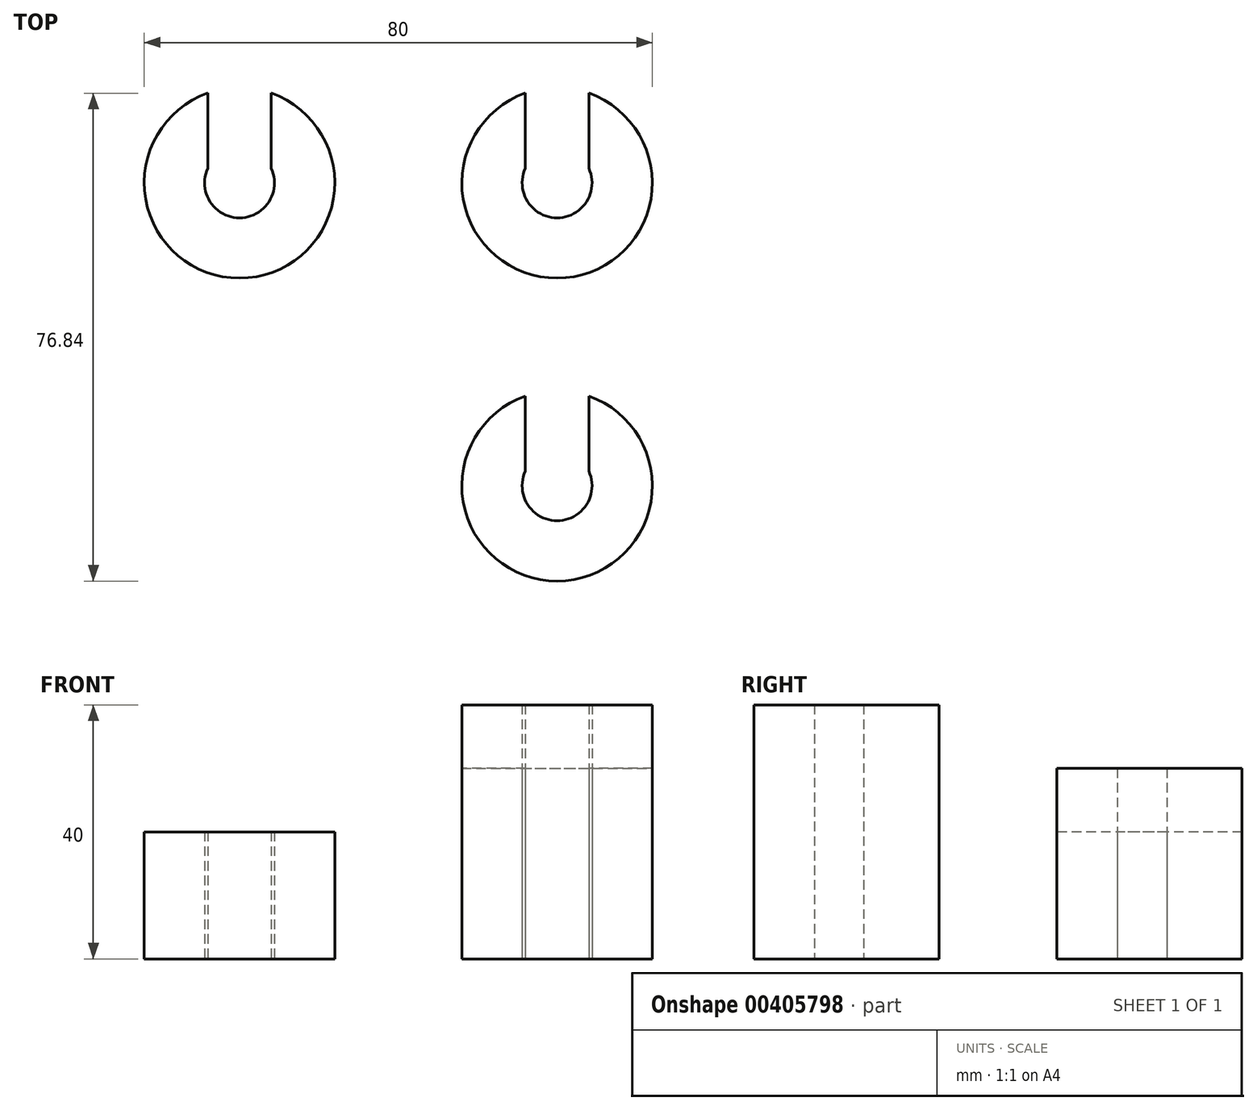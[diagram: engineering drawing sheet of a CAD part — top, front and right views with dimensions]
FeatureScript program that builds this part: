
annotation { "Feature Type Name" : "Feature", "Feature Type Description" : "" }
export const myFeature = defineFeature(function(context is Context, id is Id, definition is map)
    precondition{}
    {
        {
            var Q0;
            Q0=qCreatedBy(makeId("Top.planeOp"),FACE);
            var sketch = newSketch(context, id + "F0", { "sketchPlane" : qUnion([Q0])});
            skCircle(sketch, "E0", {"center": v(0, 0) * mm, "radius": 15 * mm});
            skCircle(sketch, "E1", {"center": v(0, 0) * mm, "radius": 5.5 * mm});
            skLineSegment(sketch, "E2", {"start": v(0, 0) * mm, "end": v(0, 15) * mm, "construction": true});
            skLineSegment(sketch, "E3", {"start": v(5, 15) * mm, "end": v(5, 2.3) * mm});
            skLineSegment(sketch, "E4", {"start": v(-5, 15) * mm, "end": v(-5, 2.3) * mm});
            skLineSegment(sketch, "E5", {"start": v(-5, 15) * mm, "end": v(5, 15) * mm});
            skSolve(sketch);
        }
        {
            var Q0;
            {var subQ0=sQuery(id+"F0.wireOp",EDGE,"E3");var subQ1=sQuery(id+"F0.wireOp",EDGE,"E0");var subQ2=makeQuery(id+"F0.imprint","INTERSECT",VERTEX,{"derivedFrom":[subQ1,subQ0]});Q0=makeQuery(id+"F0.imprint","IMPRINT",FACE,{"disambiguationData":[TD([[makeQuery(id+"F0.imprint","IMPRINT",EDGE,{"disambiguationData":[TD([[subQ2,1.0]])],"derivedFrom":subQ1}),1.0]])]});}
            extrude(context, id + "F1", {"entities" : qUnion([Q0]), "depth" : 20 * mm});
        }
        {
            var Q0;
            Q0=makeQuery(id+"F1.opExtrude","SWEPT_BODY",BODY,{"disambiguationData":[OSD([sQuery(id+"F0.wireOp",EDGE,"E0"),sQuery(id+"F0.wireOp",EDGE,"E1"),sQuery(id+"F0.wireOp",EDGE,"E3"),sQuery(id+"F0.wireOp",EDGE,"E4")])]});
            transform(context, id + "F2", {"entities" : qUnion([Q0]), "transformType" : TransformType.TRANSLATION_3D, "dx" : 50 * mm, "dy" : 0 * mm, "dz" : 0 * mm, "makeCopy" : true});
        }
        {
            var Q0;
            Q0=makeQuery(id+"F2.opPattern","COPY",FACE,{"derivedFrom":makeQuery(id+"F1.opExtrude","CAP_FACE",FACE,{"disambiguationData":[OSD([sQuery(id+"F0.wireOp",EDGE,"E0"),sQuery(id+"F0.wireOp",EDGE,"E1"),sQuery(id+"F0.wireOp",EDGE,"E3"),sQuery(id+"F0.wireOp",EDGE,"E4")])],"isStart":false}),"instanceName":"1"});
            extrude(context, id + "F3", {"entities" : qUnion([Q0]), "operationType" : NewBodyOperationType.ADD, "depth" : 10 * mm, "offsetDistance" : 25 * mm});
        }
        {
            var Q0;
            Q0=makeQuery(id+"F2.opPattern","COPY",BODY,{"derivedFrom":makeQuery(id+"F1.opExtrude","SWEPT_BODY",BODY,{"disambiguationData":[OSD([sQuery(id+"F0.wireOp",EDGE,"E0"),sQuery(id+"F0.wireOp",EDGE,"E1"),sQuery(id+"F0.wireOp",EDGE,"E3"),sQuery(id+"F0.wireOp",EDGE,"E4")])]}),"instanceName":"1"});
            transform(context, id + "F4", {"entities" : qUnion([Q0]), "transformType" : TransformType.TRANSLATION_3D, "dx" : 0 * mm, "dy" : -47.7 * mm, "dz" : 0 * mm, "makeCopy" : true});
        }
        {
            var Q0;
            Q0=makeQuery(id+"F4.opPattern","COPY",FACE,{"derivedFrom":makeQuery(id+"F3.opExtrude","CAP_FACE",FACE,{"disambiguationData":[OSD([sQuery(id+"F0.wireOp",EDGE,"E0"),sQuery(id+"F0.wireOp",EDGE,"E1"),sQuery(id+"F0.wireOp",EDGE,"E3"),sQuery(id+"F0.wireOp",EDGE,"E4")])],"isStart":false}),"instanceName":"1"});
            extrude(context, id + "F5", {"entities" : qUnion([Q0]), "operationType" : NewBodyOperationType.ADD, "depth" : 10 * mm, "offsetDistance" : 25 * mm});
        }
    });
